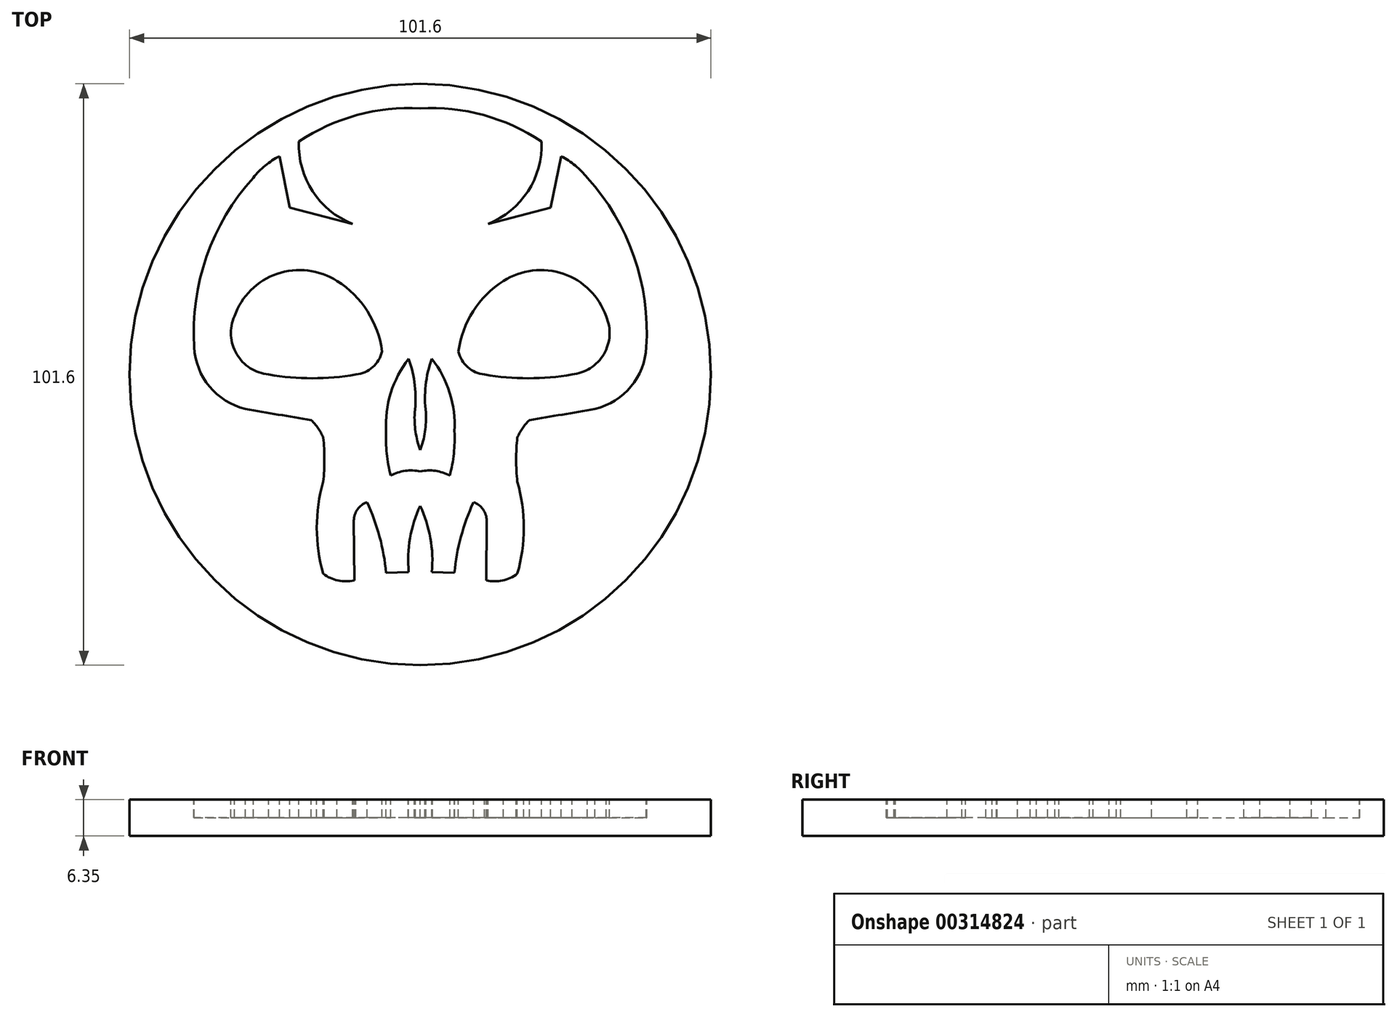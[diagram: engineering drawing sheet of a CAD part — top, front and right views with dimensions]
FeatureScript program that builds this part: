
annotation { "Feature Type Name" : "Feature", "Feature Type Description" : "" }
export const myFeature = defineFeature(function(context is Context, id is Id, definition is map)
    precondition{}
    {
        {
            var Q0;
            Q0=qCreatedBy(makeId("Top.planeOp"),FACE);
            var sketch = newSketch(context, id + "F0", { "sketchPlane" : qUnion([Q0])});
            skCircle(sketch, "E0", {"center": v(0, 0) * mm, "radius": 50.8 * mm});
            skSolve(sketch);
        }
        {
            var Q0;
            Q0 = qSketchRegion(id + "F0", true);
            extrude(context, id + "F1", {"entities" : qUnion([Q0]), "depth" : 6.35 * mm});
        }
        {
            var Q0;
            Q0=makeQuery(id+"F1.opExtrude","CAP_FACE",FACE,{"disambiguationData":[OSD([sQuery(id+"F0.wireOp",EDGE,"E0")])],"isStart":false});
            var sketch = newSketch(context, id + "F2", { "sketchPlane" : qUnion([Q0])});
            skArc(sketch, "E1", {"start": v(-32.48, 10.19) * mm, "mid": v(-32.08, 3.57) * mm, "end": v(-26.5, 0) * mm});
            skArc(sketch, "E2", {"start": v(-14.54, 16.34) * mm, "mid": v(-25, 17.61) * mm, "end": v(-32.48, 10.19) * mm});
            skArc(sketch, "E3", {"start": v(-6.68, 4.04) * mm, "mid": v(-9.24, 11.07) * mm, "end": v(-14.54, 16.34) * mm});
            skArc(sketch, "E4", {"start": v(-26.5, 0) * mm, "mid": v(-18.87, -0.66) * mm, "end": v(-11.24, 0) * mm});
            skArc(sketch, "E5", {"start": v(-11.24, 0) * mm, "mid": v(-8.3, 1.28) * mm, "end": v(-6.68, 4.04) * mm});
            skLineSegment(sketch, "E6", {"start": v(0, 0) * mm, "end": v(0, 24.45) * mm, "construction": true});
            skArc(sketch, "E7", {"start": v(-0.98, -6.68) * mm, "mid": v(-0.82, -10) * mm, "end": v(0, -13.21) * mm});
            skArc(sketch, "E8", {"start": v(-0.98, -6.68) * mm, "mid": v(-0.94, -1.9) * mm, "end": v(-2.02, 2.75) * mm});
            skArc(sketch, "E9", {"start": v(-2.02, 2.75) * mm, "mid": v(-5.15, -3.22) * mm, "end": v(-5.97, -9.9) * mm});
            skArc(sketch, "E10", {"start": v(-5.97, -9.9) * mm, "mid": v(-5.87, -13.8) * mm, "end": v(-5.17, -17.65) * mm});
            skArc(sketch, "E11", {"start": v(0, -16.92) * mm, "mid": v(-2.65, -16.83) * mm, "end": v(-5.17, -17.65) * mm});
            skArc(sketch, "E12", {"start": v(0, -22.94) * mm, "mid": v(-1.78, -28.6) * mm, "end": v(-2.02, -34.53) * mm});
            skArc(sketch, "E13", {"start": v(-5.97, -34.67) * mm, "mid": v(-7.1, -28.36) * mm, "end": v(-9.3, -22.33) * mm});
            skArc(sketch, "E14", {"start": v(-9.3, -22.33) * mm, "mid": v(-10.97, -23.55) * mm, "end": v(-11.6, -25.52) * mm});
            skArc(sketch, "E15", {"start": v(-16.96, -34.8) * mm, "mid": v(-14.38, -35.99) * mm, "end": v(-11.54, -35.96) * mm});
            skArc(sketch, "E16", {"start": v(-16.96, -18.74) * mm, "mid": v(-18.09, -26.77) * mm, "end": v(-16.96, -34.8) * mm});
            skArc(sketch, "E17", {"start": v(-16.96, -18.74) * mm, "mid": v(-16.76, -14.87) * mm, "end": v(-16.96, -11) * mm});
            skArc(sketch, "E18", {"start": v(-16.96, -11) * mm, "mid": v(-17.87, -9.38) * mm, "end": v(-19.07, -7.95) * mm});
            skArc(sketch, "E19", {"start": v(-30.55, -6) * mm, "mid": v(-24.81, -7) * mm, "end": v(-19.07, -7.95) * mm});
            skArc(sketch, "E20", {"start": v(-39.5, 4.8) * mm, "mid": v(-36.83, -2.1) * mm, "end": v(-30.55, -6) * mm});
            skArc(sketch, "E21", {"start": v(-29.2, 34.4) * mm, "mid": v(-37.34, 20.64) * mm, "end": v(-39.5, 4.8) * mm});
            skArc(sketch, "E22", {"start": v(-24.6, 38.14) * mm, "mid": v(-27.1, 36.5) * mm, "end": v(-29.2, 34.4) * mm});
            skArc(sketch, "E23", {"start": v(-21.2, 40.71) * mm, "mid": v(-18.83, 32.02) * mm, "end": v(-11.84, 26.34) * mm});
            skArc(sketch, "E24", {"start": v(0, 46.51) * mm, "mid": v(-11.07, 45.34) * mm, "end": v(-21.2, 40.71) * mm});
            skLineSegment(sketch, "E25", {"start": v(-24.6, 38.14) * mm, "end": v(-22.8, 29.13) * mm});
            skLineSegment(sketch, "E26", {"start": v(-22.8, 29.13) * mm, "end": v(-11.84, 26.34) * mm});
            skLineSegment(sketch, "E27", {"start": v(-2.02, -34.53) * mm, "end": v(-5.97, -34.67) * mm});
            skArc(sketch, "E28.MirrorCS", {"start": v(16.96, -11) * mm, "mid": v(17.87, -9.38) * mm, "end": v(19.07, -7.95) * mm});
            skArc(sketch, "E29.MirrorCS", {"start": v(6.68, 4.04) * mm, "mid": v(9.24, 11.07) * mm, "end": v(14.54, 16.34) * mm});
            skArc(sketch, "E30.MirrorCS", {"start": v(26.5, 0) * mm, "mid": v(18.87, -0.66) * mm, "end": v(11.24, 0) * mm});
            skArc(sketch, "E31.MirrorCS", {"start": v(14.54, 16.34) * mm, "mid": v(25, 17.61) * mm, "end": v(32.48, 10.19) * mm});
            skArc(sketch, "E32.MirrorCS", {"start": v(32.48, 10.19) * mm, "mid": v(32.08, 3.57) * mm, "end": v(26.5, 0) * mm});
            skArc(sketch, "E33.MirrorCS", {"start": v(11.24, 0) * mm, "mid": v(8.3, 1.28) * mm, "end": v(6.68, 4.04) * mm});
            skArc(sketch, "E34.MirrorCS", {"start": v(0, 46.51) * mm, "mid": v(11.07, 45.34) * mm, "end": v(21.2, 40.71) * mm});
            skArc(sketch, "E35.MirrorCS", {"start": v(0.98, -6.68) * mm, "mid": v(0.82, -10) * mm, "end": v(0, -13.21) * mm});
            skArc(sketch, "E36.MirrorCS", {"start": v(0.98, -6.68) * mm, "mid": v(0.94, -1.9) * mm, "end": v(2.02, 2.75) * mm});
            skArc(sketch, "E37.MirrorCS", {"start": v(24.6, 38.14) * mm, "mid": v(27.1, 36.5) * mm, "end": v(29.2, 34.4) * mm});
            skArc(sketch, "E38.MirrorCS", {"start": v(5.97, -9.9) * mm, "mid": v(5.87, -13.8) * mm, "end": v(5.17, -17.65) * mm});
            skArc(sketch, "E39.MirrorCS", {"start": v(0, -22.94) * mm, "mid": v(1.78, -28.6) * mm, "end": v(2.02, -34.53) * mm});
            skArc(sketch, "E40.MirrorCS", {"start": v(2.02, 2.75) * mm, "mid": v(5.15, -3.22) * mm, "end": v(5.97, -9.9) * mm});
            skArc(sketch, "E41.MirrorCS", {"start": v(39.5, 4.8) * mm, "mid": v(36.83, -2.1) * mm, "end": v(30.55, -6) * mm});
            skArc(sketch, "E42.MirrorCS", {"start": v(0, -16.92) * mm, "mid": v(2.65, -16.83) * mm, "end": v(5.17, -17.65) * mm});
            skArc(sketch, "E43.MirrorCS", {"start": v(16.96, -34.8) * mm, "mid": v(14.38, -35.99) * mm, "end": v(11.54, -35.96) * mm});
            skArc(sketch, "E44.MirrorCS", {"start": v(5.97, -34.67) * mm, "mid": v(7.1, -28.36) * mm, "end": v(9.3, -22.33) * mm});
            skArc(sketch, "E45.MirrorCS", {"start": v(16.96, -18.74) * mm, "mid": v(16.76, -14.87) * mm, "end": v(16.96, -11) * mm});
            skArc(sketch, "E46.MirrorCS", {"start": v(9.3, -22.33) * mm, "mid": v(10.97, -23.55) * mm, "end": v(11.6, -25.52) * mm});
            skLineSegment(sketch, "E47.MirrorCS", {"start": v(24.6, 38.14) * mm, "end": v(22.8, 29.13) * mm});
            skArc(sketch, "E48.MirrorCS", {"start": v(29.2, 34.4) * mm, "mid": v(37.34, 20.64) * mm, "end": v(39.5, 4.8) * mm});
            skArc(sketch, "E49.MirrorCS", {"start": v(21.2, 40.71) * mm, "mid": v(18.83, 32.02) * mm, "end": v(11.84, 26.34) * mm});
            skArc(sketch, "E50.MirrorCS", {"start": v(16.96, -18.74) * mm, "mid": v(18.09, -26.77) * mm, "end": v(16.96, -34.8) * mm});
            skArc(sketch, "E51.MirrorCS", {"start": v(30.55, -6) * mm, "mid": v(24.81, -7) * mm, "end": v(19.07, -7.95) * mm});
            skLineSegment(sketch, "E52.MirrorCS", {"start": v(2.02, -34.53) * mm, "end": v(5.97, -34.67) * mm});
            skLineSegment(sketch, "E53.MirrorCS", {"start": v(22.8, 29.13) * mm, "end": v(11.84, 26.34) * mm});
            skLineSegment(sketch, "E54", {"start": v(-11.54, -35.96) * mm, "end": v(-11.6, -25.52) * mm});
            skLineSegment(sketch, "E55", {"start": v(11.6, -25.52) * mm, "end": v(11.54, -35.96) * mm});
            skSolve(sketch);
        }
        {
            var Q0;
            Q0 = qSketchRegion(id + "F2", true);
            extrude(context, id + "F3", {"entities" : qUnion([Q0]), "operationType" : NewBodyOperationType.REMOVE, "oppositeDirection" : true, "depth" : 3.17 * mm});
        }
    });
